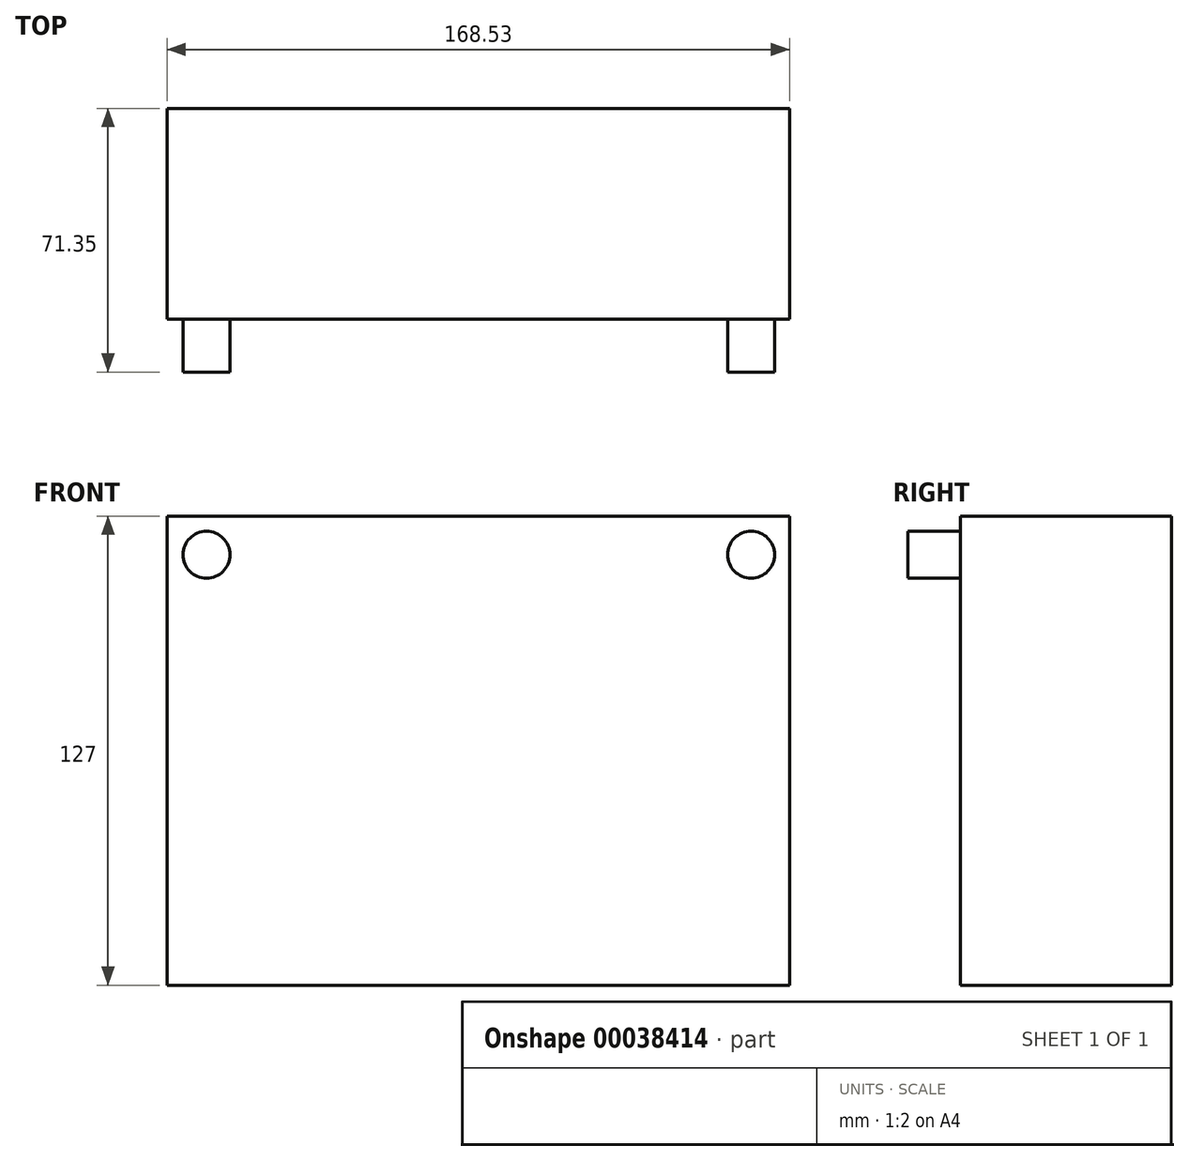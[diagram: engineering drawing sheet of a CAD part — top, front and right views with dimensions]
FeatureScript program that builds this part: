
annotation { "Feature Type Name" : "Feature", "Feature Type Description" : "" }
export const myFeature = defineFeature(function(context is Context, id is Id, definition is map)
    precondition{}
    {
        {
            var Q0;
            Q0=qCreatedBy(makeId("Top.planeOp"),FACE);
            var sketch = newSketch(context, id + "F0", { "sketchPlane" : qUnion([Q0])});
            skLineSegment(sketch, "E0.bottom", {"start": v(-63.62, -17.5) * mm, "end": v(104.9, -17.5) * mm});
            skLineSegment(sketch, "E0.top", {"start": v(-63.62, 39.6) * mm, "end": v(104.9, 39.6) * mm});
            skLineSegment(sketch, "E0.left", {"start": v(-63.62, -17.5) * mm, "end": v(-63.62, 39.6) * mm});
            skLineSegment(sketch, "E0.right", {"start": v(104.9, -17.5) * mm, "end": v(104.9, 39.6) * mm});
            skSolve(sketch);
        }
        {
            var Q0;
            Q0 = qSketchRegion(id + "F0", true);
            extrude(context, id + "F1", {"entities" : qUnion([Q0]), "depth" : 127 * mm});
        }
        {
            var Q0;
            Q0=qCreatedBy(makeId("Front.planeOp"),FACE);
            var sketch = newSketch(context, id + "F2", { "sketchPlane" : qUnion([Q0])});
            skCircle(sketch, "E1", {"center": v(-52.95, 116.51) * mm, "radius": 6.35 * mm});
            skCircle(sketch, "E2", {"center": v(94.49, 116.54) * mm, "radius": 6.35 * mm});
            skSolve(sketch);
        }
        {
            var Q0;
            Q0=sQuery(id+"F2.wireOp",EDGE,"E2");
            extrude(context, id + "F3", {"bodyType" : ToolBodyType.SURFACE, "surfaceEntities" : qUnion([Q0]), "depth" : 31.75 * mm});
        }
        {
            var Q0;
            Q0 = qSketchRegion(id + "F2", true);
            extrude(context, id + "F4", {"entities" : qUnion([Q0]), "operationType" : NewBodyOperationType.ADD, "depth" : 31.75 * mm});
        }
    });
